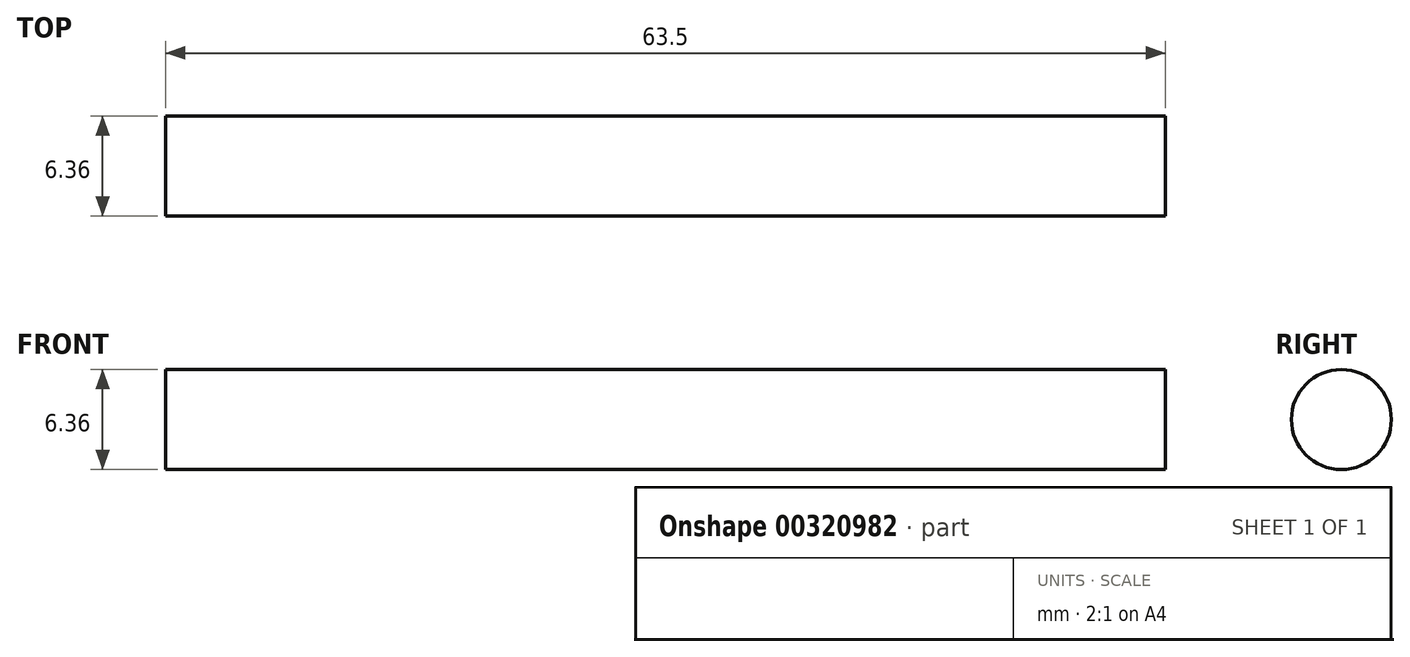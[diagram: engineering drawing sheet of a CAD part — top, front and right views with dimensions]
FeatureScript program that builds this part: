
annotation { "Feature Type Name" : "Feature", "Feature Type Description" : "" }
export const myFeature = defineFeature(function(context is Context, id is Id, definition is map)
    precondition{}
    {
        {
            var Q0;
            Q0=qCreatedBy(makeId("Right.planeOp"),FACE);
            var sketch = newSketch(context, id + "F0", { "sketchPlane" : qUnion([Q0])});
            skCircle(sketch, "E0", {"center": v(0, 0) * mm, "radius": 3.18 * mm});
            skSolve(sketch);
        }
        {
            var Q0;
            Q0=makeQuery(id+"F0.imprint","IMPRINT",FACE,{"disambiguationData":[TD([[makeQuery(id+"F0.imprint","IMPRINT",EDGE,{"derivedFrom":sQuery(id+"F0.wireOp",EDGE,"E0")}),1.0]])]});
            extrude(context, id + "F1", {"entities" : qUnion([Q0]), "endBound" : BoundingType.SYMMETRIC, "depth" : 63.5 * mm});
        }
    });
